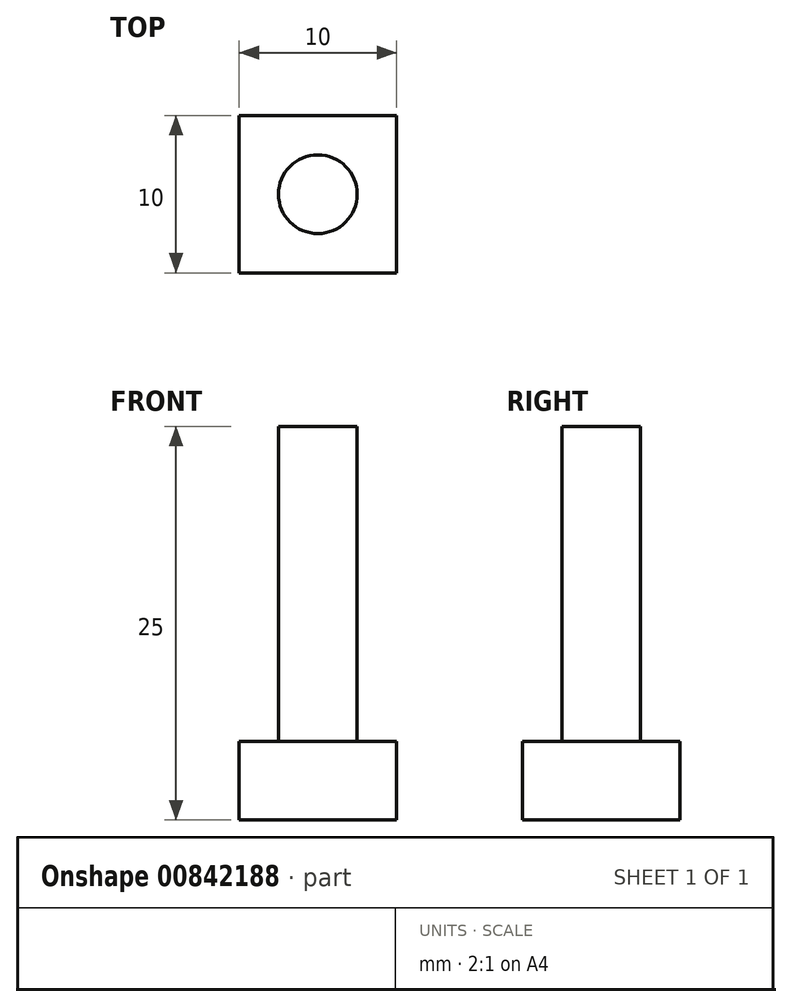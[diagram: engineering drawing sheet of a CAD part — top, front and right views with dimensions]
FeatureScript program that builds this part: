
annotation { "Feature Type Name" : "Feature", "Feature Type Description" : "" }
export const myFeature = defineFeature(function(context is Context, id is Id, definition is map)
    precondition{}
    {
        {
            var Q0;
            Q0=qCreatedBy(makeId("Top.planeOp"),FACE);
            var sketch = newSketch(context, id + "F0", { "sketchPlane" : qUnion([Q0])});
            skCircle(sketch, "E0", {"center": v(0, 0) * mm, "radius": 2.5 * mm});
            skSolve(sketch);
        }
        {
            var Q0;
            Q0 = qSketchRegion(id + "F0", true);
            extrude(context, id + "F1", {"entities" : qUnion([Q0]), "depth" : 20 * mm, "offsetDistance" : 25 * mm});
        }
        {
            var Q0;
            Q0=makeQuery(id+"F1.opExtrude","CAP_FACE",FACE,{"disambiguationData":[OSD([sQuery(id+"F0.wireOp",EDGE,"E0")])],"isStart":true});
            var sketch = newSketch(context, id + "F2", { "sketchPlane" : qUnion([Q0])});
            skLineSegment(sketch, "E1.bottom", {"start": v(5, 5) * mm, "end": v(-5, 5) * mm});
            skLineSegment(sketch, "E1.top", {"start": v(5, -5) * mm, "end": v(-5, -5) * mm});
            skLineSegment(sketch, "E1.left", {"start": v(5, 5) * mm, "end": v(5, -5) * mm});
            skLineSegment(sketch, "E1.right", {"start": v(-5, 5) * mm, "end": v(-5, -5) * mm});
            skPoint(sketch, "E1.middle", {"position": v(0, 0) * mm});
            skSolve(sketch);
        }
        {
            var Q0;
            Q0 = qSketchRegion(id + "F2", true);
            extrude(context, id + "F3", {"entities" : qUnion([Q0]), "operationType" : NewBodyOperationType.ADD, "depth" : 5 * mm, "offsetDistance" : 25 * mm});
        }
    });
